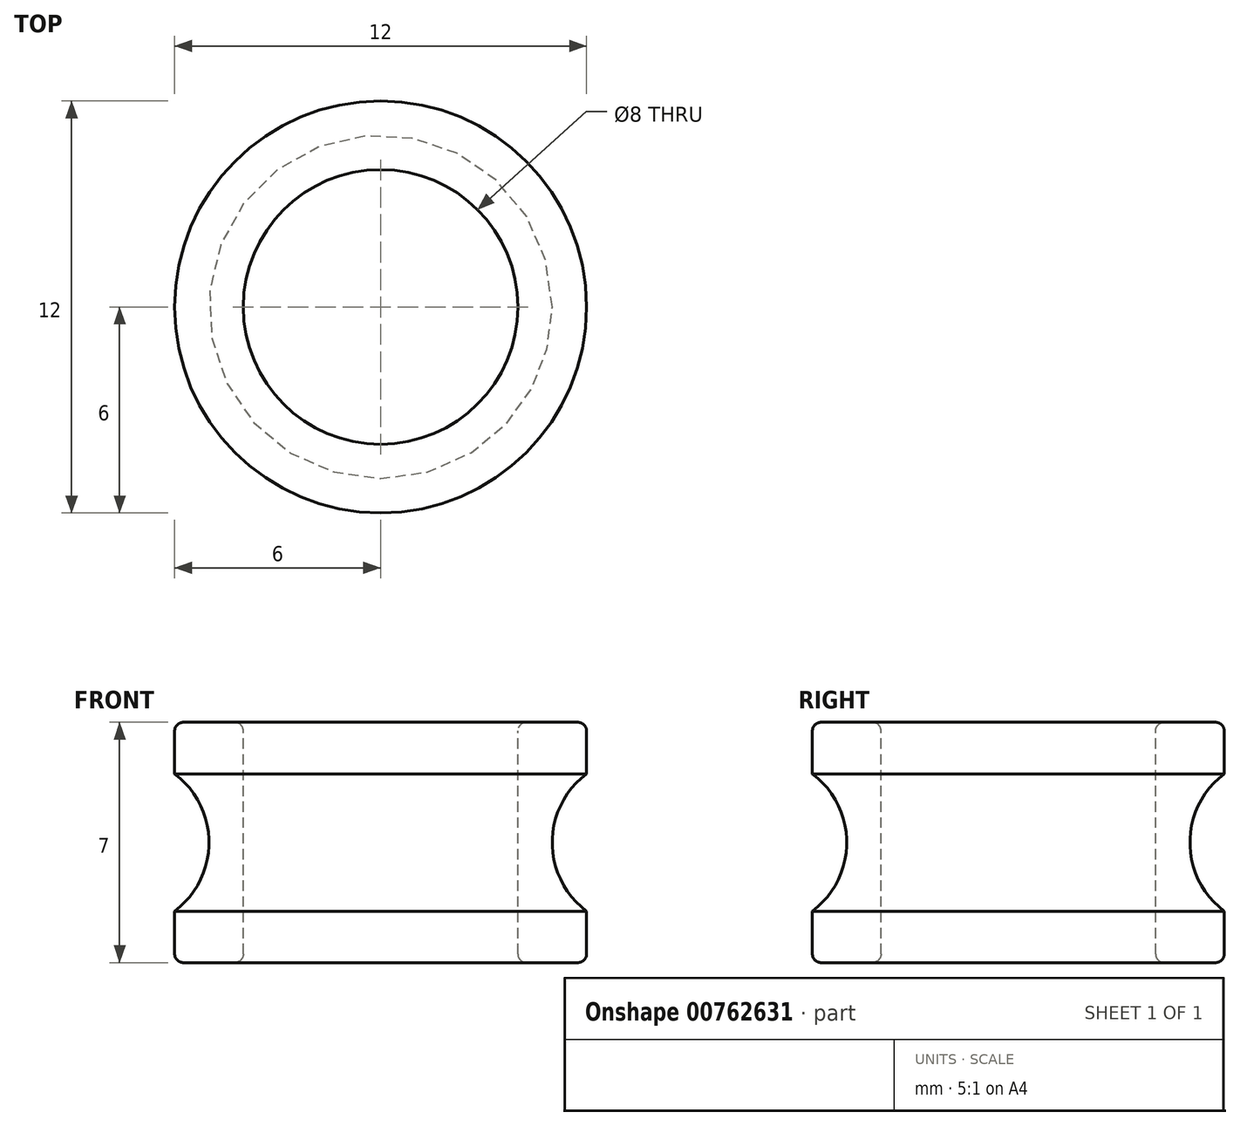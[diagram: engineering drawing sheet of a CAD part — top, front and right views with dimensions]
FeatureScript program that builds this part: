
annotation { "Feature Type Name" : "Feature", "Feature Type Description" : "" }
export const myFeature = defineFeature(function(context is Context, id is Id, definition is map)
    precondition{}
    {
        {
            var Q0;
            Q0=qCreatedBy(makeId("Front.planeOp"),FACE);
            var sketch = newSketch(context, id + "F0", { "sketchPlane" : qUnion([Q0])});
            skLineSegment(sketch, "E0", {"start": v(0, 4.7) * mm, "end": v(0, -4.02) * mm});
            skLineSegment(sketch, "E1", {"start": v(4, 0) * mm, "end": v(6, 0) * mm});
            skLineSegment(sketch, "E2", {"start": v(4, 0) * mm, "end": v(4, 3.25) * mm});
            skLineSegment(sketch, "E3", {"start": v(4, 0) * mm, "end": v(4, -3.25) * mm});
            skLineSegment(sketch, "E4", {"start": v(0, 0) * mm, "end": v(4, 0) * mm});
            skLineSegment(sketch, "E5", {"start": v(4.25, 3.5) * mm, "end": v(5.75, 3.5) * mm});
            skLineSegment(sketch, "E6", {"start": v(4.25, -3.5) * mm, "end": v(5.75, -3.5) * mm});
            skLineSegment(sketch, "E7", {"start": v(6, -3.25) * mm, "end": v(6, -2) * mm});
            skArc(sketch, "E8", {"start": v(6, 2) * mm, "mid": v(5, 0) * mm, "end": v(6, -2) * mm});
            skPoint(sketch, "E9.end.orphan", {"position": v(11, -3.5) * mm});
            skPoint(sketch, "E10.start.orphan", {"position": v(11, 3.5) * mm});
            skPoint(sketch, "E11.start.orphan", {"position": v(9, 3.5) * mm});
            skPoint(sketch, "E12.trimOffspring.end.orphan", {"position": v(9, -3.5) * mm});
            skPoint(sketch, "E13.trimOffspring.end.orphan", {"position": v(11, 0) * mm});
            skLineSegment(sketch, "E14.trimOffspring", {"start": v(6, 2) * mm, "end": v(6, 3.25) * mm});
            skPoint(sketch, "E15.visualSharp", {"position": v(4, 3.5) * mm});
            skArc(sketch, "E15.filletArc", {"start": v(4.25, 3.5) * mm, "mid": v(4.07, 3.43) * mm, "end": v(4, 3.25) * mm});
            skPoint(sketch, "E16.visualSharp", {"position": v(4, -3.5) * mm});
            skArc(sketch, "E16.filletArc", {"start": v(4, -3.25) * mm, "mid": v(4.07, -3.43) * mm, "end": v(4.25, -3.5) * mm});
            skPoint(sketch, "E17.visualSharp", {"position": v(6, -3.5) * mm});
            skArc(sketch, "E17.filletArc", {"start": v(5.75, -3.5) * mm, "mid": v(5.93, -3.43) * mm, "end": v(6, -3.25) * mm});
            skPoint(sketch, "E18.visualSharp", {"position": v(6, 3.5) * mm});
            skArc(sketch, "E18.filletArc", {"start": v(6, 3.25) * mm, "mid": v(5.93, 3.43) * mm, "end": v(5.75, 3.5) * mm});
            skSolve(sketch);
        }
        {
            var Q0;
            Q0=qSketchRegion(id+"F0",true);
            var Q1;
            Q1=sQuery(id+"F0.wireOp",EDGE,"E0");
            revolve(context, id + "F1", {"surfaceOperationType" : NewSurfaceOperationType.NEW, "entities" : qUnion([Q0]), "axis" : qUnion([Q1]), "revolveType" : RevolveType.FULL});
        }
    });
